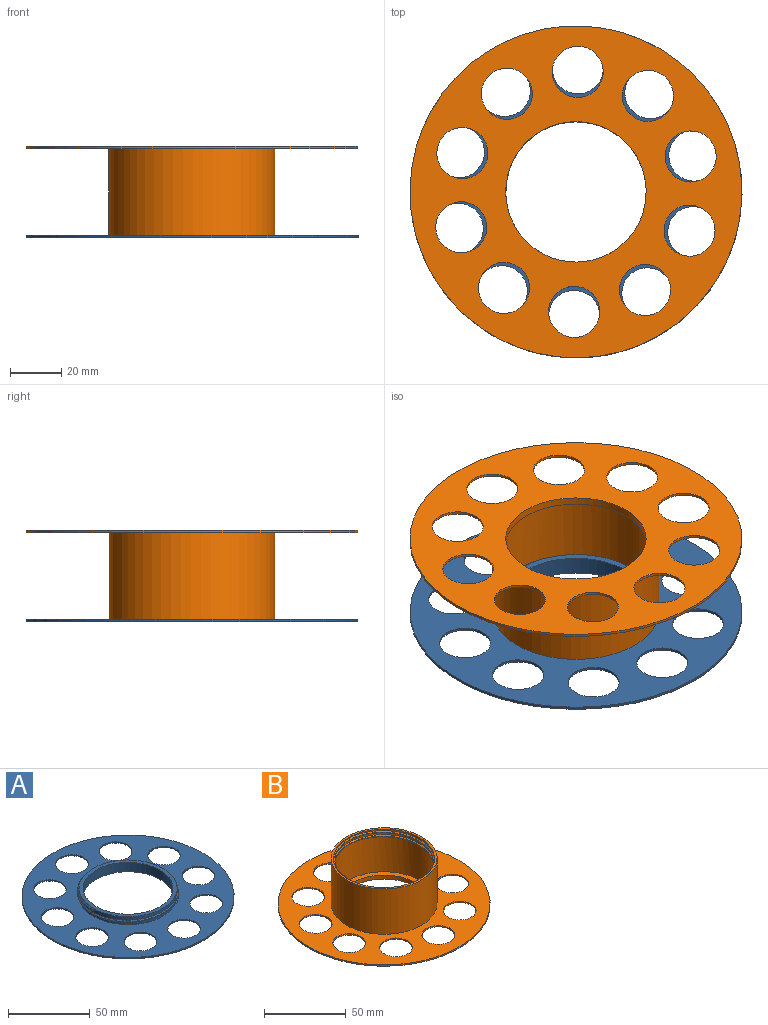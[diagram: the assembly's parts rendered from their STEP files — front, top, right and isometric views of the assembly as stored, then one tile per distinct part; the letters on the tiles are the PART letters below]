
ASSEMBLY  parts=2 mates=1
PART A: 23 faces, bbox 130x130x7 mm
  f0: plane 130x130mm, normal (0,0,1), area 7271mm2, adj f1,f3,f4,f5,f6,f7,f8,f9
  f1: cylinder r=30.1mm len=60.2mm, axis (0,0,-1), area 640.9mm2, adj f0,f15,f16,f17,f19,f20,f21,f22
  f2: cylinder r=27.5mm len=55mm, axis (0,0,-1), area 1209.5mm2, adj f14,f15
  f3: cylinder r=10mm len=20mm, axis (0,0,-1), area 62.8mm2, adj f0,f14
  f4: cylinder r=10mm len=20mm, axis (0,0,-1), area 62.8mm2, adj f0,f14
  f5: cylinder r=10mm len=20mm, axis (0,0,-1), area 62.8mm2, adj f0,f14
  f6: cylinder r=10mm len=20mm, axis (0,0,-1), area 62.8mm2, adj f0,f14
  f7: cylinder r=10mm len=20mm, axis (0,0,-1), area 62.8mm2, adj f0,f14
  f8: cylinder r=10mm len=20mm, axis (0,0,-1), area 62.8mm2, adj f0,f14
  f9: cylinder r=10mm len=20mm, axis (0,0,-1), area 62.8mm2, adj f0,f14
  f10: cylinder r=10mm len=20mm, axis (0,0,-1), area 62.8mm2, adj f0,f14
  f11: cylinder r=10mm len=20mm, axis (0,0,-1), area 62.8mm2, adj f0,f14
  f12: cylinder r=10mm len=20mm, axis (0,0,-1), area 62.8mm2, adj f0,f14
  f13: cylinder r=65mm len=130mm, axis (0,0,-1), area 408.4mm2, adj f0,f14
  f14: plane 130x130mm, normal (0,0,-1), area 7755.8mm2, adj f2,f3,f4,f5,f6,f7,f8,f9
  f15: plane 60.2x60.2mm, normal (0,0,1), area 470.5mm2, adj f1,f2
  f16: plane 1x0.65mm, normal (-0.87,-0.5,0), area 0.5mm2, adj f0,f1,f18,f19
  f17: bspline ~71.25x61.7mm, area 287.9mm2, adj f0,f1,f18,f22
  f18: cylinder r=30.85mm len=61.7mm, axis (0,0,-1), area 129.2mm2, adj f16,f17,f19,f20
  f19: bspline ~71.25x61.7mm, area 306.3mm2, adj f1,f16,f18,f21
  f20: cylinder r=0.75mm len=0.76mm, axis (0,0,-1), area 0.5mm2, adj f1,f18,f21,f22
  f21: cone r=0.75mm half-angle=51.3deg, axis (0,0,-1), area 0.6mm2, adj f1,f19,f20
  f22: cone r=0mm half-angle=51.3deg, axis (0,0,1), area 0.6mm2, adj f1,f17,f20
PART B: 26 faces, bbox 130x130x35 mm
  f0: cylinder r=31mm len=62mm, axis (0,0,-1), area 5421.3mm2, adj f1,f17,f19,f20,f25
  f1: cylinder r=31mm len=62mm, axis (0,0,-1), area 291.5mm2, adj f0,f16,f20,f21,f22,f23
  f2: cylinder r=10mm len=20mm, axis (0,0,-1), area 62.8mm2, adj f13,f14
  f3: cylinder r=10mm len=20mm, axis (0,0,-1), area 62.8mm2, adj f13,f14
  f4: cylinder r=10mm len=20mm, axis (0,0,-1), area 62.8mm2, adj f13,f14
  f5: cylinder r=10mm len=20mm, axis (0,0,-1), area 62.8mm2, adj f13,f14
  f6: cylinder r=10mm len=20mm, axis (0,0,-1), area 62.8mm2, adj f13,f14
  f7: cylinder r=10mm len=20mm, axis (0,0,-1), area 62.8mm2, adj f13,f14
  f8: cylinder r=10mm len=20mm, axis (0,0,-1), area 62.8mm2, adj f13,f14
  f9: cylinder r=10mm len=20mm, axis (0,0,-1), area 62.8mm2, adj f13,f14
  f10: cylinder r=10mm len=20mm, axis (0,0,-1), area 62.8mm2, adj f13,f14
  f11: cylinder r=10mm len=20mm, axis (0,0,-1), area 62.8mm2, adj f13,f14
  f12: cylinder r=65mm len=130mm, axis (0,0,-1), area 408.4mm2, adj f13,f14
  f13: plane 130x130mm, normal (0,0,1), area 6813.3mm2, adj f2,f3,f4,f5,f6,f7,f8,f9
  f14: plane 130x130mm, normal (0,0,-1), area 7755.8mm2, adj f2,f3,f4,f5,f6,f7,f8,f9
  f15: cylinder r=32.5mm len=65mm, axis (0,0,-1), area 6942.9mm2, adj f13,f16
  f16: plane 65x65mm, normal (0,0,1), area 299.2mm2, adj f1,f15
  f17: plane 1.6x0.64mm, normal (-0.87,-0.5,0), area 0.7mm2, adj f0,f18,f19,f20
  f18: cylinder r=30.27mm len=60.53mm, axis (0,0,-1), area 135.1mm2, adj f17,f19,f20,f21
  f19: bspline ~71.59x62mm, area 301.3mm2, adj f0,f17,f18,f23
  f20: bspline ~71.59x62mm, area 301.1mm2, adj f0,f1,f17,f18,f22
  f21: cylinder r=0.73mm len=0.73mm, axis (0,0,1), area 0.5mm2, adj f1,f18,f22,f23
  f22: cone r=0mm half-angle=51.3deg, axis (0,0,-1), area 0.7mm2, adj f1,f20,f21
  f23: cone r=0.73mm half-angle=51.3deg, axis (0,0,1), area 0.5mm2, adj f1,f19,f21
  f24: cylinder r=27.5mm len=55mm, axis (0,0,-1), area 518.4mm2, adj f14,f25
  f25: plane 62x62mm, normal (0,0,1), area 643.2mm2, adj f0,f24
PLACE A rot(axis=(0,0,-1),0.8deg) t=(43.18,30.97,2.74)mm
PLACE B rot(axis=(0.01,1,0),180deg) t=(43.13,31,38.74)mm
MATE fastened A.f0 <-> B.f0  axis (0,0,1) through (43.13,31,3.74)mm
